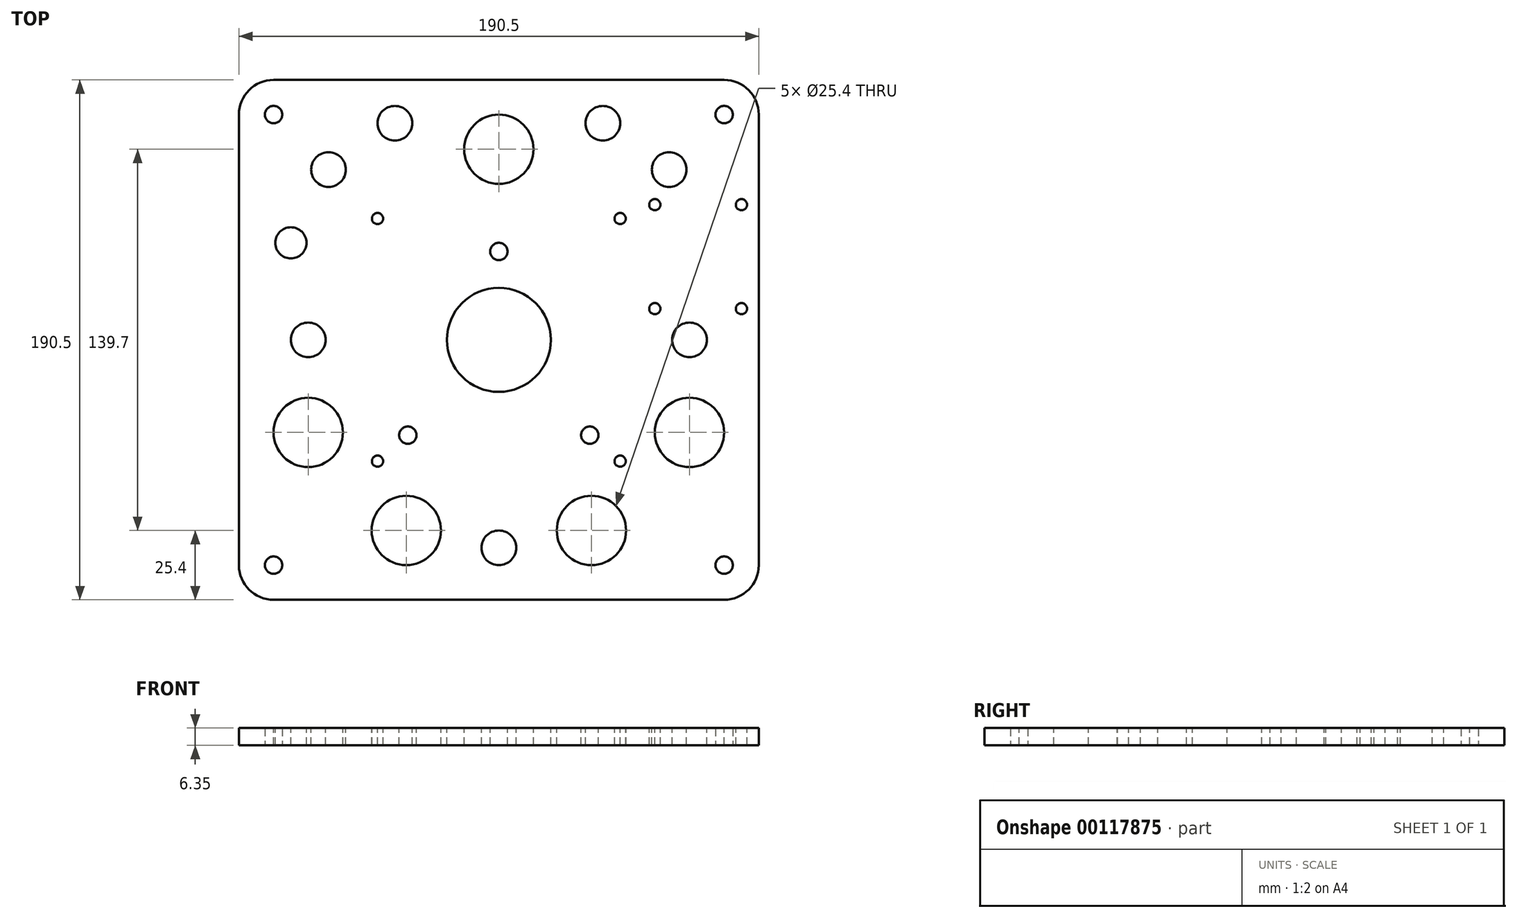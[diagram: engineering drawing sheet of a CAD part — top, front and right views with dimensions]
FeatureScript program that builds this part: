
annotation { "Feature Type Name" : "Feature", "Feature Type Description" : "" }
export const myFeature = defineFeature(function(context is Context, id is Id, definition is map)
    precondition{}
    {
        {
            var Q0;
            Q0=qCreatedBy(makeId("Top.planeOp"),FACE);
            var sketch = newSketch(context, id + "F0", { "sketchPlane" : qUnion([Q0])});
            skLineSegment(sketch, "E0.bottom", {"start": v(95.25, 95.25) * mm, "end": v(-95.25, 95.25) * mm});
            skLineSegment(sketch, "E0.top", {"start": v(95.25, -95.25) * mm, "end": v(-95.25, -95.25) * mm});
            skLineSegment(sketch, "E0.left", {"start": v(95.25, 95.25) * mm, "end": v(95.25, -95.25) * mm});
            skLineSegment(sketch, "E0.right", {"start": v(-95.25, 95.25) * mm, "end": v(-95.25, -95.25) * mm});
            skPoint(sketch, "E0.middle", {"position": v(0, 0) * mm});
            skLineSegment(sketch, "E1", {"start": v(0, 95.25) * mm, "end": v(0, -95.25) * mm, "construction": true});
            skLineSegment(sketch, "E2", {"start": v(-95.25, 0) * mm, "end": v(95.25, 0) * mm, "construction": true});
            skCircle(sketch, "E3", {"center": v(-82.55, 82.55) * mm, "radius": 3.18 * mm});
            skCircle(sketch, "E4.MirrorC", {"center": v(82.55, 82.55) * mm, "radius": 3.18 * mm});
            skCircle(sketch, "E5.MirrorC", {"center": v(-82.55, -82.55) * mm, "radius": 3.18 * mm});
            skCircle(sketch, "E6.MirrorC", {"center": v(82.55, -82.55) * mm, "radius": 3.18 * mm});
            skSolve(sketch);
        }
        {
            var Q0;
            Q0=qSketchRegion(id+"F0",true);
            extrude(context, id + "F1", {"entities" : qUnion([Q0]), "depth" : 6.35 * mm});
        }
        {
            var Q0;
            Q0=makeQuery(id+"F1.opExtrude","CAP_FACE",FACE,{"disambiguationData":[OSD([sQuery(id+"F0.wireOp",EDGE,"E0.bottom"),sQuery(id+"F0.wireOp",EDGE,"E0.top"),sQuery(id+"F0.wireOp",EDGE,"E0.left"),sQuery(id+"F0.wireOp",EDGE,"E0.right"),sQuery(id+"F0.wireOp",EDGE,"E3"),sQuery(id+"F0.wireOp",EDGE,"E4.MirrorC"),sQuery(id+"F0.wireOp",EDGE,"E5.MirrorC"),sQuery(id+"F0.wireOp",EDGE,"E6.MirrorC")])],"isStart":false});
            var sketch = newSketch(context, id + "F2", { "sketchPlane" : qUnion([Q0])});
            skLineSegment(sketch, "E7.bottom", {"start": v(57.15, 49.53) * mm, "end": v(88.9, 49.53) * mm});
            skLineSegment(sketch, "E7.top", {"start": v(57.15, 11.43) * mm, "end": v(88.9, 11.43) * mm});
            skLineSegment(sketch, "E7.left", {"start": v(57.15, 49.53) * mm, "end": v(57.15, 11.43) * mm});
            skLineSegment(sketch, "E7.right", {"start": v(88.9, 49.53) * mm, "end": v(88.9, 11.43) * mm});
            skCircle(sketch, "E8", {"center": v(57.15, 49.53) * mm, "radius": 2.06 * mm});
            skCircle(sketch, "E9", {"center": v(88.9, 49.53) * mm, "radius": 2.06 * mm});
            skCircle(sketch, "E10", {"center": v(88.9, 11.43) * mm, "radius": 2.06 * mm});
            skCircle(sketch, "E11", {"center": v(57.15, 11.43) * mm, "radius": 2.06 * mm});
            skSolve(sketch);
        }
        {
            var Q0;
            {var subQ0=sQuery(id+"F2.wireOp",EDGE,"E7.left");var subQ1=sQuery(id+"F2.wireOp",EDGE,"E7.bottom");var subQ2=makeQuery(id+"F2.imprint","INTERSECT",VERTEX,{"derivedFrom":[subQ1,subQ0]});Q0=makeQuery(id+"F2.imprint","IMPRINT",FACE,{"disambiguationData":[TD([[makeQuery(id+"F2.imprint","IMPRINT",EDGE,{"disambiguationData":[TD([[subQ2,-1.0]])],"derivedFrom":subQ1}),1.0]])]});}
            var Q1;
            {var subQ0=sQuery(id+"F2.wireOp",EDGE,"E7.left");var subQ1=sQuery(id+"F2.wireOp",EDGE,"E7.bottom");var subQ2=makeQuery(id+"F2.imprint","INTERSECT",VERTEX,{"derivedFrom":[subQ1,subQ0]});Q1=makeQuery(id+"F2.imprint","IMPRINT",FACE,{"disambiguationData":[TD([[makeQuery(id+"F2.imprint","IMPRINT",EDGE,{"disambiguationData":[TD([[subQ2,-1.0]])],"derivedFrom":subQ1}),-1.0]])]});}
            var Q2;
            {var subQ0=sQuery(id+"F2.wireOp",EDGE,"E7.right");var subQ1=sQuery(id+"F2.wireOp",EDGE,"E7.bottom");var subQ2=makeQuery(id+"F2.imprint","INTERSECT",VERTEX,{"derivedFrom":[subQ1,subQ0]});Q2=makeQuery(id+"F2.imprint","IMPRINT",FACE,{"disambiguationData":[TD([[makeQuery(id+"F2.imprint","IMPRINT",EDGE,{"disambiguationData":[TD([[subQ2,1.0]])],"derivedFrom":subQ1}),-1.0]])]});}
            var Q3;
            {var subQ0=sQuery(id+"F2.wireOp",EDGE,"E7.right");var subQ1=sQuery(id+"F2.wireOp",EDGE,"E7.bottom");var subQ2=makeQuery(id+"F2.imprint","INTERSECT",VERTEX,{"derivedFrom":[subQ1,subQ0]});Q3=makeQuery(id+"F2.imprint","IMPRINT",FACE,{"disambiguationData":[TD([[makeQuery(id+"F2.imprint","IMPRINT",EDGE,{"disambiguationData":[TD([[subQ2,1.0]])],"derivedFrom":subQ1}),1.0]])]});}
            var Q4;
            {var subQ0=sQuery(id+"F2.wireOp",EDGE,"E7.left");var subQ1=sQuery(id+"F2.wireOp",EDGE,"E7.top");var subQ2=makeQuery(id+"F2.imprint","INTERSECT",VERTEX,{"derivedFrom":[subQ1,subQ0]});Q4=makeQuery(id+"F2.imprint","IMPRINT",FACE,{"disambiguationData":[TD([[makeQuery(id+"F2.imprint","IMPRINT",EDGE,{"disambiguationData":[TD([[subQ2,-1.0]])],"derivedFrom":subQ1}),1.0]])]});}
            var Q5;
            {var subQ0=sQuery(id+"F2.wireOp",EDGE,"E7.left");var subQ1=sQuery(id+"F2.wireOp",EDGE,"E7.top");var subQ2=makeQuery(id+"F2.imprint","INTERSECT",VERTEX,{"derivedFrom":[subQ1,subQ0]});Q5=makeQuery(id+"F2.imprint","IMPRINT",FACE,{"disambiguationData":[TD([[makeQuery(id+"F2.imprint","IMPRINT",EDGE,{"disambiguationData":[TD([[subQ2,-1.0]])],"derivedFrom":subQ1}),-1.0]])]});}
            var Q6;
            {var subQ0=sQuery(id+"F2.wireOp",EDGE,"E7.right");var subQ1=sQuery(id+"F2.wireOp",EDGE,"E7.top");var subQ2=makeQuery(id+"F2.imprint","INTERSECT",VERTEX,{"derivedFrom":[subQ1,subQ0]});Q6=makeQuery(id+"F2.imprint","IMPRINT",FACE,{"disambiguationData":[TD([[makeQuery(id+"F2.imprint","IMPRINT",EDGE,{"disambiguationData":[TD([[subQ2,1.0]])],"derivedFrom":subQ1}),1.0]])]});}
            var Q7;
            {var subQ0=sQuery(id+"F2.wireOp",EDGE,"E7.right");var subQ1=sQuery(id+"F2.wireOp",EDGE,"E7.top");var subQ2=makeQuery(id+"F2.imprint","INTERSECT",VERTEX,{"derivedFrom":[subQ1,subQ0]});Q7=makeQuery(id+"F2.imprint","IMPRINT",FACE,{"disambiguationData":[TD([[makeQuery(id+"F2.imprint","IMPRINT",EDGE,{"disambiguationData":[TD([[subQ2,1.0]])],"derivedFrom":subQ1}),-1.0]])]});}
            extrude(context, id + "F3", {"entities" : qUnion([Q0, Q1, Q2, Q3, Q4, Q5, Q6, Q7]), "operationType" : NewBodyOperationType.REMOVE, "endBound" : BoundingType.THROUGH_ALL, "oppositeDirection" : true, "depth" : 25.4 * mm});
        }
        {
            var Q0;
            Q0=makeQuery(id+"F1.opExtrude","CAP_FACE",FACE,{"disambiguationData":[OSD([sQuery(id+"F0.wireOp",EDGE,"E0.bottom"),sQuery(id+"F0.wireOp",EDGE,"E0.top"),sQuery(id+"F0.wireOp",EDGE,"E0.left"),sQuery(id+"F0.wireOp",EDGE,"E0.right"),sQuery(id+"F0.wireOp",EDGE,"E3"),sQuery(id+"F0.wireOp",EDGE,"E4.MirrorC"),sQuery(id+"F0.wireOp",EDGE,"E5.MirrorC"),sQuery(id+"F0.wireOp",EDGE,"E6.MirrorC")])],"isStart":false});
            var sketch = newSketch(context, id + "F4", { "sketchPlane" : qUnion([Q0])});
            skLineSegment(sketch, "E12.bottom", {"start": v(-44.45, -44.45) * mm, "end": v(44.45, -44.45) * mm});
            skLineSegment(sketch, "E12.top", {"start": v(-44.45, 44.45) * mm, "end": v(44.45, 44.45) * mm});
            skLineSegment(sketch, "E12.left", {"start": v(-44.45, -44.45) * mm, "end": v(-44.45, 44.45) * mm});
            skLineSegment(sketch, "E12.right", {"start": v(44.45, -44.45) * mm, "end": v(44.45, 44.45) * mm});
            skCircle(sketch, "E13", {"center": v(-44.45, 44.45) * mm, "radius": 2.06 * mm});
            skCircle(sketch, "E14", {"center": v(44.45, 44.45) * mm, "radius": 2.06 * mm});
            skCircle(sketch, "E15", {"center": v(44.45, -44.45) * mm, "radius": 2.06 * mm});
            skCircle(sketch, "E16", {"center": v(-44.45, -44.45) * mm, "radius": 2.06 * mm});
            skLineSegment(sketch, "E17", {"start": v(0, 44.45) * mm, "end": v(0, -44.45) * mm, "construction": true});
            skLineSegment(sketch, "E18", {"start": v(-44.45, 0) * mm, "end": v(44.45, 0) * mm, "construction": true});
            skSolve(sketch);
        }
        {
            var Q0;
            {var subQ0=sQuery(id+"F4.wireOp",EDGE,"E12.left");var subQ1=sQuery(id+"F4.wireOp",EDGE,"E12.bottom");var subQ2=makeQuery(id+"F4.imprint","INTERSECT",VERTEX,{"derivedFrom":[subQ1,subQ0]});Q0=makeQuery(id+"F4.imprint","IMPRINT",FACE,{"disambiguationData":[TD([[makeQuery(id+"F4.imprint","IMPRINT",EDGE,{"disambiguationData":[TD([[subQ2,-1.0]])],"derivedFrom":subQ1}),1.0]])]});}
            var Q1;
            {var subQ0=sQuery(id+"F4.wireOp",EDGE,"E12.left");var subQ1=sQuery(id+"F4.wireOp",EDGE,"E12.bottom");var subQ2=makeQuery(id+"F4.imprint","INTERSECT",VERTEX,{"derivedFrom":[subQ1,subQ0]});Q1=makeQuery(id+"F4.imprint","IMPRINT",FACE,{"disambiguationData":[TD([[makeQuery(id+"F4.imprint","IMPRINT",EDGE,{"disambiguationData":[TD([[subQ2,-1.0]])],"derivedFrom":subQ1}),-1.0]])]});}
            var Q2;
            {var subQ0=sQuery(id+"F4.wireOp",EDGE,"E12.right");var subQ1=sQuery(id+"F4.wireOp",EDGE,"E12.bottom");var subQ2=makeQuery(id+"F4.imprint","INTERSECT",VERTEX,{"derivedFrom":[subQ1,subQ0]});Q2=makeQuery(id+"F4.imprint","IMPRINT",FACE,{"disambiguationData":[TD([[makeQuery(id+"F4.imprint","IMPRINT",EDGE,{"disambiguationData":[TD([[subQ2,1.0]])],"derivedFrom":subQ1}),1.0]])]});}
            var Q3;
            {var subQ0=sQuery(id+"F4.wireOp",EDGE,"E12.right");var subQ1=sQuery(id+"F4.wireOp",EDGE,"E12.bottom");var subQ2=makeQuery(id+"F4.imprint","INTERSECT",VERTEX,{"derivedFrom":[subQ1,subQ0]});Q3=makeQuery(id+"F4.imprint","IMPRINT",FACE,{"disambiguationData":[TD([[makeQuery(id+"F4.imprint","IMPRINT",EDGE,{"disambiguationData":[TD([[subQ2,1.0]])],"derivedFrom":subQ1}),-1.0]])]});}
            var Q4;
            {var subQ0=sQuery(id+"F4.wireOp",EDGE,"E12.left");var subQ1=sQuery(id+"F4.wireOp",EDGE,"E12.top");var subQ2=makeQuery(id+"F4.imprint","INTERSECT",VERTEX,{"derivedFrom":[subQ1,subQ0]});Q4=makeQuery(id+"F4.imprint","IMPRINT",FACE,{"disambiguationData":[TD([[makeQuery(id+"F4.imprint","IMPRINT",EDGE,{"disambiguationData":[TD([[subQ2,-1.0]])],"derivedFrom":subQ1}),1.0]])]});}
            var Q5;
            {var subQ0=sQuery(id+"F4.wireOp",EDGE,"E12.left");var subQ1=sQuery(id+"F4.wireOp",EDGE,"E12.top");var subQ2=makeQuery(id+"F4.imprint","INTERSECT",VERTEX,{"derivedFrom":[subQ1,subQ0]});Q5=makeQuery(id+"F4.imprint","IMPRINT",FACE,{"disambiguationData":[TD([[makeQuery(id+"F4.imprint","IMPRINT",EDGE,{"disambiguationData":[TD([[subQ2,-1.0]])],"derivedFrom":subQ1}),-1.0]])]});}
            var Q6;
            {var subQ0=sQuery(id+"F4.wireOp",EDGE,"E12.right");var subQ1=sQuery(id+"F4.wireOp",EDGE,"E12.top");var subQ2=makeQuery(id+"F4.imprint","INTERSECT",VERTEX,{"derivedFrom":[subQ1,subQ0]});Q6=makeQuery(id+"F4.imprint","IMPRINT",FACE,{"disambiguationData":[TD([[makeQuery(id+"F4.imprint","IMPRINT",EDGE,{"disambiguationData":[TD([[subQ2,1.0]])],"derivedFrom":subQ1}),-1.0]])]});}
            var Q7;
            {var subQ0=sQuery(id+"F4.wireOp",EDGE,"E12.right");var subQ1=sQuery(id+"F4.wireOp",EDGE,"E12.top");var subQ2=makeQuery(id+"F4.imprint","INTERSECT",VERTEX,{"derivedFrom":[subQ1,subQ0]});Q7=makeQuery(id+"F4.imprint","IMPRINT",FACE,{"disambiguationData":[TD([[makeQuery(id+"F4.imprint","IMPRINT",EDGE,{"disambiguationData":[TD([[subQ2,1.0]])],"derivedFrom":subQ1}),1.0]])]});}
            extrude(context, id + "F5", {"entities" : qUnion([Q0, Q1, Q2, Q3, Q4, Q5, Q6, Q7]), "operationType" : NewBodyOperationType.REMOVE, "endBound" : BoundingType.THROUGH_ALL, "oppositeDirection" : true, "depth" : 25.4 * mm});
        }
        {
            var Q0;
            Q0=makeQuery(id+"F1.opExtrude","CAP_FACE",FACE,{"disambiguationData":[OSD([sQuery(id+"F0.wireOp",EDGE,"E0.bottom"),sQuery(id+"F0.wireOp",EDGE,"E0.top"),sQuery(id+"F0.wireOp",EDGE,"E0.left"),sQuery(id+"F0.wireOp",EDGE,"E0.right"),sQuery(id+"F0.wireOp",EDGE,"E3"),sQuery(id+"F0.wireOp",EDGE,"E4.MirrorC"),sQuery(id+"F0.wireOp",EDGE,"E5.MirrorC"),sQuery(id+"F0.wireOp",EDGE,"E6.MirrorC")])],"isStart":false});
            var sketch = newSketch(context, id + "F6", { "sketchPlane" : qUnion([Q0])});
            skLineSegment(sketch, "E19", {"start": v(-44.45, 44.45) * mm, "end": v(-44.45, -44.45) * mm, "construction": true});
            skLineSegment(sketch, "E20", {"start": v(-44.45, -44.45) * mm, "end": v(44.45, -44.45) * mm, "construction": true});
            skLineSegment(sketch, "E21", {"start": v(44.45, -44.45) * mm, "end": v(44.45, 44.45) * mm, "construction": true});
            skLineSegment(sketch, "E22", {"start": v(44.45, 44.45) * mm, "end": v(-44.45, 44.45) * mm, "construction": true});
            skLineSegment(sketch, "E23", {"start": v(-44.45, -34.92) * mm, "end": v(44.45, -34.92) * mm, "construction": true});
            skLineSegment(sketch, "E24", {"start": v(-44.45, 32.39) * mm, "end": v(44.45, 32.39) * mm, "construction": true});
            skLineSegment(sketch, "E25", {"start": v(0, 44.45) * mm, "end": v(0, -44.45) * mm, "construction": true});
            skCircle(sketch, "E26", {"center": v(0, 0) * mm, "radius": 19.05 * mm});
            skCircle(sketch, "E27", {"center": v(-33.34, -34.92) * mm, "radius": 3.18 * mm});
            skCircle(sketch, "E28", {"center": v(33.34, -34.92) * mm, "radius": 3.18 * mm});
            skCircle(sketch, "E29", {"center": v(0, 32.39) * mm, "radius": 3.18 * mm});
            skSolve(sketch);
        }
        {
            var Q0;
            Q0=makeQuery(id+"F6.imprint","IMPRINT",FACE,{"disambiguationData":[TD([[makeQuery(id+"F6.imprint","IMPRINT",EDGE,{"derivedFrom":sQuery(id+"F6.wireOp",EDGE,"E27")}),1.0]])]});
            var Q1;
            Q1=makeQuery(id+"F6.imprint","IMPRINT",FACE,{"disambiguationData":[TD([[makeQuery(id+"F6.imprint","IMPRINT",EDGE,{"derivedFrom":sQuery(id+"F6.wireOp",EDGE,"E28")}),1.0]])]});
            var Q2;
            Q2=makeQuery(id+"F6.imprint","IMPRINT",FACE,{"disambiguationData":[TD([[makeQuery(id+"F6.imprint","IMPRINT",EDGE,{"derivedFrom":sQuery(id+"F6.wireOp",EDGE,"E29")}),1.0]])]});
            var Q3;
            Q3=makeQuery(id+"F6.imprint","IMPRINT",FACE,{"disambiguationData":[TD([[makeQuery(id+"F6.imprint","IMPRINT",EDGE,{"derivedFrom":sQuery(id+"F6.wireOp",EDGE,"E26")}),1.0]])]});
            extrude(context, id + "F7", {"entities" : qUnion([Q0, Q1, Q2, Q3]), "operationType" : NewBodyOperationType.REMOVE, "endBound" : BoundingType.THROUGH_ALL, "oppositeDirection" : true, "depth" : 25.4 * mm});
        }
        {
            var Q0;
            Q0=makeQuery(id+"F1.opExtrude","SWEPT_EDGE",EDGE,{"disambiguationData":[OSD([sQuery(id+"F0.wireOp",EDGE,"E0.bottom"),sQuery(id+"F0.wireOp",EDGE,"E0.right")])]});
            var Q1;
            Q1=makeQuery(id+"F1.opExtrude","SWEPT_EDGE",EDGE,{"disambiguationData":[OSD([sQuery(id+"F0.wireOp",EDGE,"E0.bottom"),sQuery(id+"F0.wireOp",EDGE,"E0.left")])]});
            var Q2;
            Q2=makeQuery(id+"F1.opExtrude","SWEPT_EDGE",EDGE,{"disambiguationData":[OSD([sQuery(id+"F0.wireOp",EDGE,"E0.top"),sQuery(id+"F0.wireOp",EDGE,"E0.left")])]});
            var Q3;
            Q3=makeQuery(id+"F1.opExtrude","SWEPT_EDGE",EDGE,{"disambiguationData":[OSD([sQuery(id+"F0.wireOp",EDGE,"E0.top"),sQuery(id+"F0.wireOp",EDGE,"E0.right")])]});
            fillet(context, id + "F8", {"entities" : qUnion([Q0, Q1, Q2, Q3]), "radius" : 12.7 * mm, "tangentPropagation" : true, "allowEdgeOverflow" : false});
        }
        {
            var Q0;
            Q0=makeQuery(id+"F1.opExtrude","CAP_FACE",FACE,{"disambiguationData":[OSD([sQuery(id+"F0.wireOp",EDGE,"E0.bottom"),sQuery(id+"F0.wireOp",EDGE,"E0.top"),sQuery(id+"F0.wireOp",EDGE,"E0.left"),sQuery(id+"F0.wireOp",EDGE,"E0.right"),sQuery(id+"F0.wireOp",EDGE,"E3"),sQuery(id+"F0.wireOp",EDGE,"E4.MirrorC"),sQuery(id+"F0.wireOp",EDGE,"E5.MirrorC"),sQuery(id+"F0.wireOp",EDGE,"E6.MirrorC")])],"isStart":false});
            var sketch = newSketch(context, id + "F9", { "sketchPlane" : qUnion([Q0])});
            skLineSegment(sketch, "E30", {"start": v(-91.53, -91.53) * mm, "end": v(91.53, 91.53) * mm, "construction": true});
            skLineSegment(sketch, "E31", {"start": v(-91.53, 91.53) * mm, "end": v(91.53, -91.53) * mm, "construction": true});
            skLineSegment(sketch, "E32", {"start": v(-44.45, 44.45) * mm, "end": v(44.45, 44.45) * mm, "construction": true});
            skLineSegment(sketch, "E33", {"start": v(44.45, 44.45) * mm, "end": v(44.45, -44.45) * mm, "construction": true});
            skLineSegment(sketch, "E34", {"start": v(44.45, -44.45) * mm, "end": v(-44.45, -44.45) * mm, "construction": true});
            skLineSegment(sketch, "E35", {"start": v(-44.45, -44.45) * mm, "end": v(-44.45, 44.45) * mm, "construction": true});
            skLineSegment(sketch, "E36", {"start": v(-95.25, 0) * mm, "end": v(95.25, 0) * mm, "construction": true});
            skLineSegment(sketch, "E37", {"start": v(0, -95.25) * mm, "end": v(0, 95.25) * mm, "construction": true});
            skCircle(sketch, "E38", {"center": v(62.41, 62.41) * mm, "radius": 6.35 * mm});
            skCircle(sketch, "E39", {"center": v(0, 69.85) * mm, "radius": 12.7 * mm});
            skCircle(sketch, "E40.MirrorC", {"center": v(-62.41, 62.41) * mm, "radius": 6.35 * mm});
            skCircle(sketch, "E41", {"center": v(69.85, 0) * mm, "radius": 6.35 * mm});
            skCircle(sketch, "E42.MirrorC", {"center": v(-69.85, 0) * mm, "radius": 6.35 * mm});
            skSolve(sketch);
        }
        {
            var Q0;
            Q0 = qSketchRegion(id + "F9", true);
            extrude(context, id + "F10", {"entities" : qUnion([Q0]), "operationType" : NewBodyOperationType.REMOVE, "endBound" : BoundingType.THROUGH_ALL, "oppositeDirection" : true, "depth" : 25.4 * mm});
        }
        {
            var Q0;
            Q0=makeQuery(id+"F1.opExtrude","CAP_FACE",FACE,{"disambiguationData":[OSD([sQuery(id+"F0.wireOp",EDGE,"E0.bottom"),sQuery(id+"F0.wireOp",EDGE,"E0.top"),sQuery(id+"F0.wireOp",EDGE,"E0.left"),sQuery(id+"F0.wireOp",EDGE,"E0.right"),sQuery(id+"F0.wireOp",EDGE,"E3"),sQuery(id+"F0.wireOp",EDGE,"E4.MirrorC"),sQuery(id+"F0.wireOp",EDGE,"E5.MirrorC"),sQuery(id+"F0.wireOp",EDGE,"E6.MirrorC")])],"isStart":false});
            var sketch = newSketch(context, id + "F11", { "sketchPlane" : qUnion([Q0])});
            skLineSegment(sketch, "E43", {"start": v(0, 0) * mm, "end": v(0, -95.25) * mm, "construction": true});
            skLineSegment(sketch, "E44", {"start": v(-95.25, 0) * mm, "end": v(95.25, 0) * mm, "construction": true});
            skLineSegment(sketch, "E45", {"start": v(-91.53, -91.53) * mm, "end": v(0, 0) * mm, "construction": true});
            skLineSegment(sketch, "E46", {"start": v(0, 0) * mm, "end": v(91.53, -91.53) * mm, "construction": true});
            skCircle(sketch, "E47", {"center": v(-69.85, -33.93) * mm, "radius": 12.7 * mm});
            skCircle(sketch, "E48.MirrorC", {"center": v(-33.93, -69.85) * mm, "radius": 12.7 * mm});
            skCircle(sketch, "E49.MirrorC", {"center": v(69.85, -33.93) * mm, "radius": 12.7 * mm});
            skCircle(sketch, "E50.MirrorC", {"center": v(33.93, -69.85) * mm, "radius": 12.7 * mm});
            skSolve(sketch);
        }
        {
            var Q0;
            Q0 = qSketchRegion(id + "F11", true);
            extrude(context, id + "F12", {"entities" : qUnion([Q0]), "operationType" : NewBodyOperationType.REMOVE, "endBound" : BoundingType.THROUGH_ALL, "oppositeDirection" : true, "depth" : 25.4 * mm});
        }
        {
            var Q0;
            Q0=makeQuery(id+"F1.opExtrude","CAP_FACE",FACE,{"disambiguationData":[OSD([sQuery(id+"F0.wireOp",EDGE,"E0.bottom"),sQuery(id+"F0.wireOp",EDGE,"E0.top"),sQuery(id+"F0.wireOp",EDGE,"E0.left"),sQuery(id+"F0.wireOp",EDGE,"E0.right"),sQuery(id+"F0.wireOp",EDGE,"E3"),sQuery(id+"F0.wireOp",EDGE,"E4.MirrorC"),sQuery(id+"F0.wireOp",EDGE,"E5.MirrorC"),sQuery(id+"F0.wireOp",EDGE,"E6.MirrorC")])],"isStart":false});
            var sketch = newSketch(context, id + "F13", { "sketchPlane" : qUnion([Q0])});
            skCircle(sketch, "E51", {"center": v(-76.2, 35.56) * mm, "radius": 5.72 * mm});
            skCircle(sketch, "E52", {"center": v(-38.1, 79.38) * mm, "radius": 6.35 * mm});
            skLineSegment(sketch, "E53", {"start": v(-82.55, 95.25) * mm, "end": v(144.58, 95.25) * mm, "construction": true});
            skLineSegment(sketch, "E54", {"start": v(0, 95.25) * mm, "end": v(0, -95.25) * mm, "construction": true});
            skCircle(sketch, "E55.MirrorC", {"center": v(38.1, 79.38) * mm, "radius": 6.35 * mm});
            skCircle(sketch, "E56", {"center": v(0, -76.2) * mm, "radius": 6.35 * mm});
            skLineSegment(sketch, "E57", {"start": v(0, -76.2) * mm, "end": v(-95.25, -76.2) * mm, "construction": true});
            skLineSegment(sketch, "E58", {"start": v(-95.25, -76.2) * mm, "end": v(95.25, -76.2) * mm, "construction": true});
            skSolve(sketch);
        }
        {
            var Q0;
            Q0 = qSketchRegion(id + "F13", true);
            extrude(context, id + "F14", {"entities" : qUnion([Q0]), "operationType" : NewBodyOperationType.REMOVE, "endBound" : BoundingType.THROUGH_ALL, "oppositeDirection" : true, "depth" : 25.4 * mm});
        }
    });
